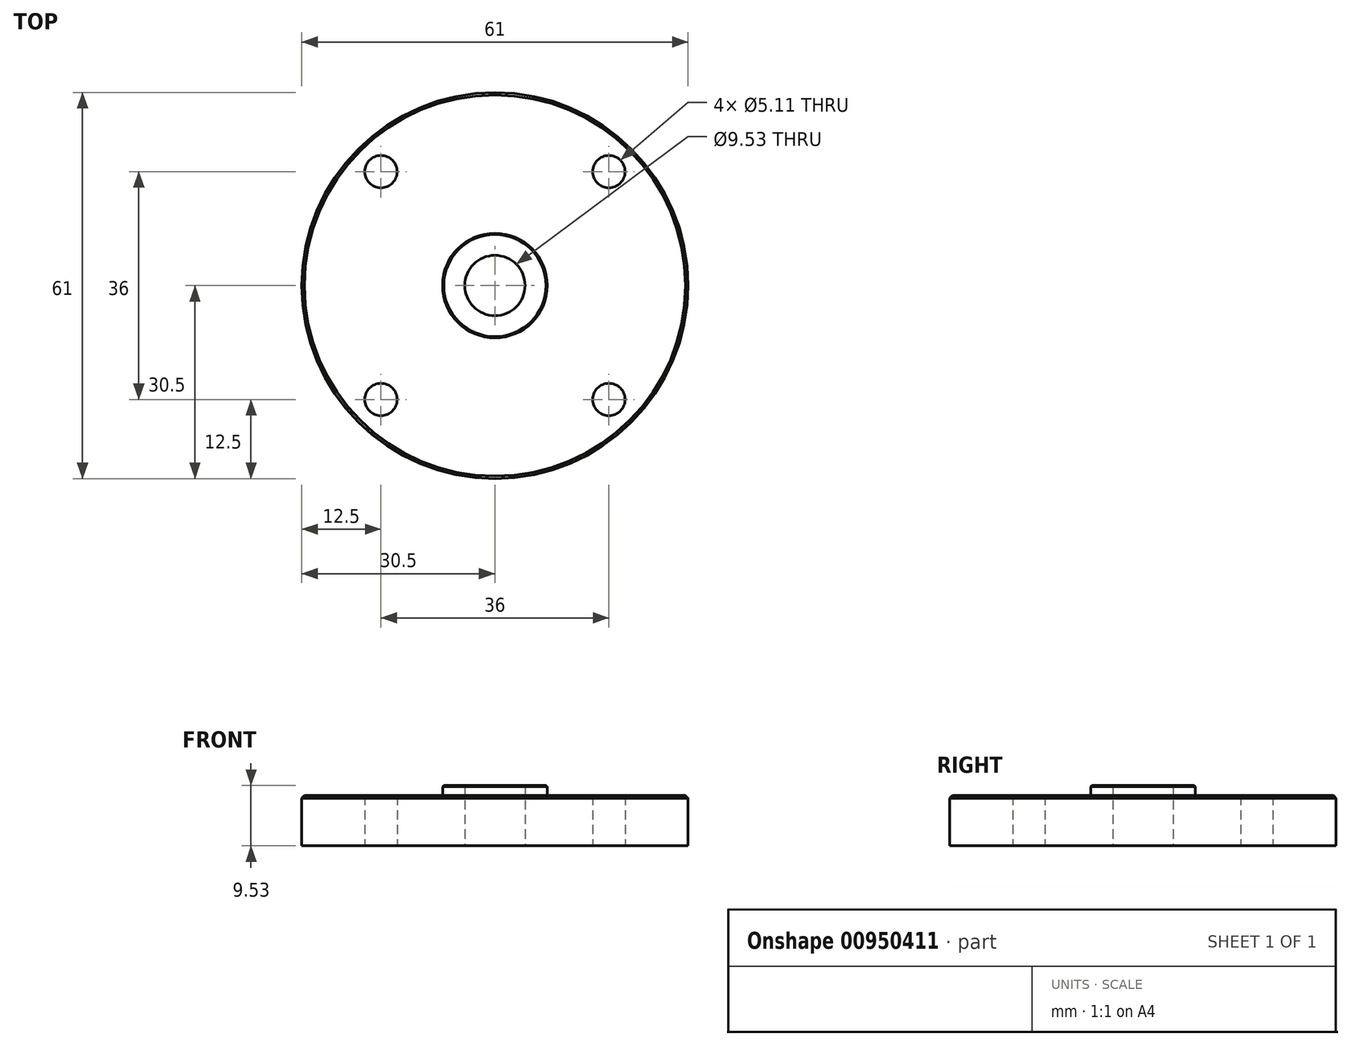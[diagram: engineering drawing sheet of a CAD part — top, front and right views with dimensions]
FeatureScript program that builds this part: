
annotation { "Feature Type Name" : "Feature", "Feature Type Description" : "" }
export const myFeature = defineFeature(function(context is Context, id is Id, definition is map)
    precondition{}
    {
        {
            var Q0;
            Q0=qCreatedBy(makeId("Top.planeOp"),FACE);
            var sketch = newSketch(context, id + "F0", { "sketchPlane" : qUnion([Q0])});
            skCircle(sketch, "E0", {"center": v(0, 0) * mm, "radius": 30.5 * mm});
            skLineSegment(sketch, "E1", {"start": v(0, 38.79) * mm, "end": v(0, -41.36) * mm, "construction": true});
            skLineSegment(sketch, "E2", {"start": v(-38.04, 0) * mm, "end": v(42.7, 0) * mm, "construction": true});
            skCircle(sketch, "E3", {"center": v(-18, 18) * mm, "radius": 2.56 * mm});
            skLineSegment(sketch, "E4", {"start": v(-18, 18) * mm, "end": v(-18, 0) * mm});
            skLineSegment(sketch, "E5", {"start": v(-18, 18) * mm, "end": v(0, 18) * mm});
            skCircle(sketch, "E6", {"center": v(18, 18) * mm, "radius": 2.56 * mm});
            skCircle(sketch, "E7", {"center": v(18, -18) * mm, "radius": 2.56 * mm});
            skCircle(sketch, "E8", {"center": v(-18, -18) * mm, "radius": 2.56 * mm});
            skCircle(sketch, "E9", {"center": v(0, 0) * mm, "radius": 4.77 * mm});
            skCircle(sketch, "E10", {"center": v(0, 0) * mm, "radius": 8.27 * mm});
            skSolve(sketch);
        }
        {
            var Q0;
            Q0=makeQuery(id+"F0.imprint","IMPRINT",FACE,{"disambiguationData":[TD([[makeQuery(id+"F0.imprint","IMPRINT",EDGE,{"derivedFrom":sQuery(id+"F0.wireOp",EDGE,"E0")}),1.0]])]});
            extrude(context, id + "F1", {"entities" : qUnion([Q0]), "depth" : 7.94 * mm, "offsetDistance" : 25 * mm});
        }
        {
            var Q0;
            Q0=makeQuery(id+"F1.opExtrude","CAP_EDGE",EDGE,{"disambiguationData":[OSD([sQuery(id+"F0.wireOp",EDGE,"E0")])],"isStart":false});
            chamfer(context, id + "F2", {"entities" : qUnion([Q0]), "width" : .4 * mm, "tangentPropagation" : true});
        }
        {
            var Q0;
            Q0=makeQuery(id+"F0.imprint","IMPRINT",FACE,{"disambiguationData":[TD([[makeQuery(id+"F0.imprint","IMPRINT",EDGE,{"derivedFrom":sQuery(id+"F0.wireOp",EDGE,"E9")}),-1.0]])]});
            var Q1;
            Q1=sQuery(id+"F0.wireOp",EDGE,"E10");
            var Q2;
            Q2=sQuery(id+"F0.wireOp",EDGE,"E9");
            extrude(context, id + "F3", {"entities" : qUnion([Q0]), "operationType" : NewBodyOperationType.ADD, "surfaceEntities" : qUnion([Q1, Q2]), "depth" : 9.53 * mm, "offsetDistance" : 25 * mm});
        }
        {
            var Q0;
            Q0=makeQuery(id+"F3.opExtrude","CAP_EDGE",EDGE,{"disambiguationData":[OSD([sQuery(id+"F0.wireOp",EDGE,"E10")])],"isStart":false});
            chamfer(context, id + "F4", {"entities" : qUnion([Q0]), "width" : .2 * mm, "tangentPropagation" : true});
        }
    });
